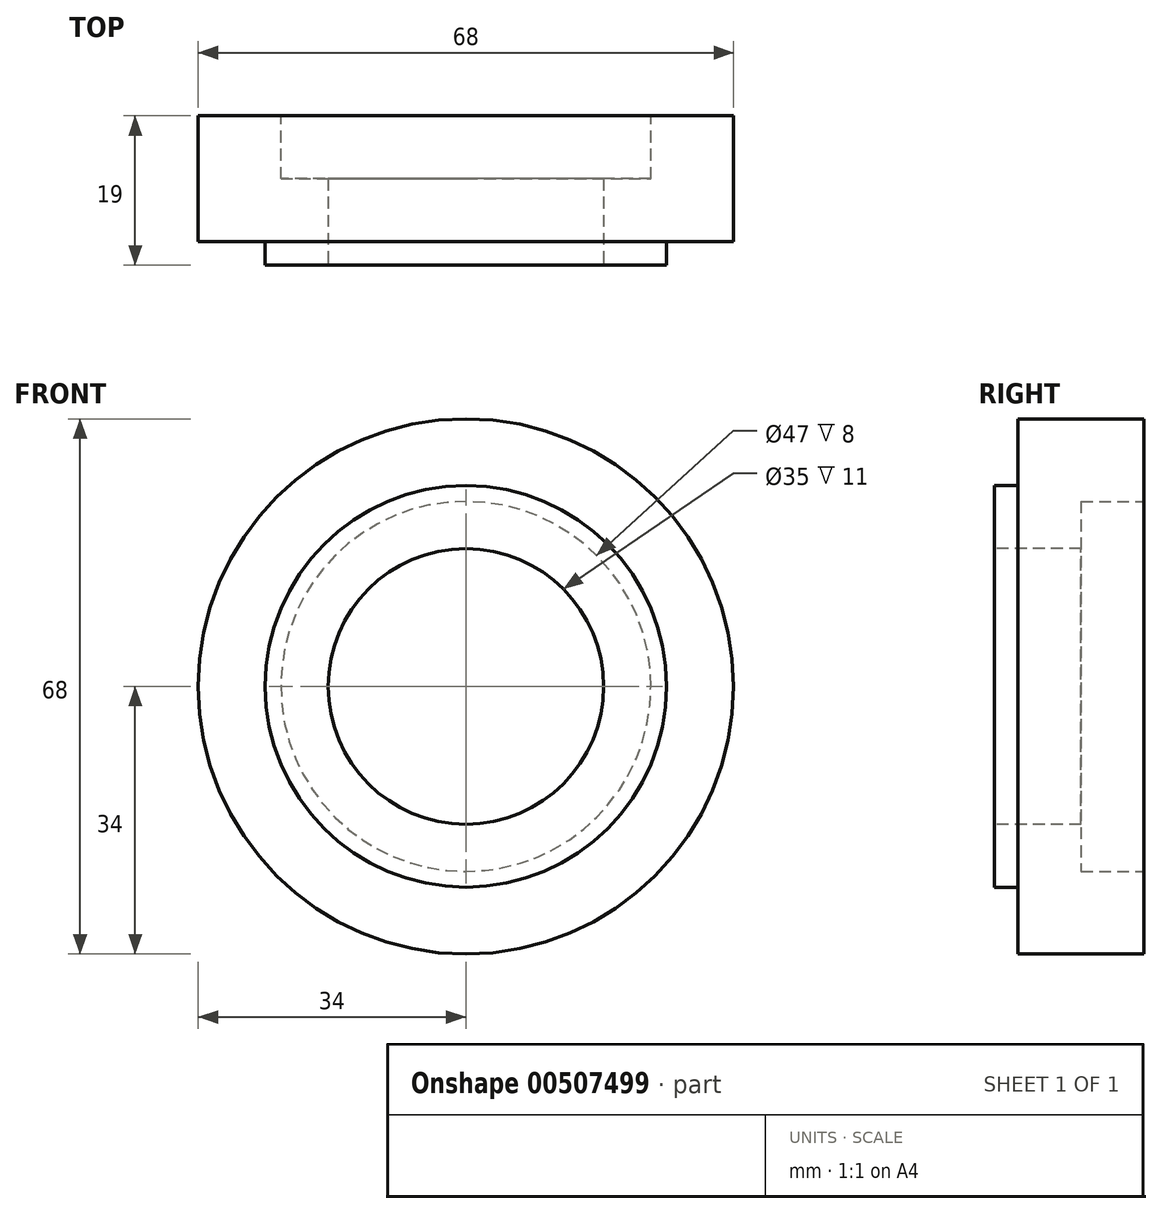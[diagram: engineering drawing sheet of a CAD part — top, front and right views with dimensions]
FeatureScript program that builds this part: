
annotation { "Feature Type Name" : "Feature", "Feature Type Description" : "" }
export const myFeature = defineFeature(function(context is Context, id is Id, definition is map)
    precondition{}
    {
        {
            var Q0;
            Q0=qCreatedBy(makeId("Front.planeOp"),FACE);
            var sketch = newSketch(context, id + "F0", { "sketchPlane" : qUnion([Q0])});
            skCircle(sketch, "E0", {"center": v(0, 0) * mm, "radius": 34 * mm});
            skSolve(sketch);
        }
        {
            var Q0;
            Q0 = qSketchRegion(id + "F0", true);
            extrude(context, id + "F1", {"entities" : qUnion([Q0]), "depth" : 16 * mm});
        }
        {
            var Q0;
            Q0=makeQuery(id+"F1.opExtrude","CAP_FACE",FACE,{"disambiguationData":[OSD([sQuery(id+"F0.wireOp",EDGE,"E0")])],"isStart":false});
            var sketch = newSketch(context, id + "F2", { "sketchPlane" : qUnion([Q0])});
            skCircle(sketch, "E1", {"center": v(0, 0) * mm, "radius": 25.5 * mm});
            skSolve(sketch);
        }
        {
            var Q0;
            Q0 = qSketchRegion(id + "F2", true);
            extrude(context, id + "F3", {"entities" : qUnion([Q0]), "operationType" : NewBodyOperationType.ADD, "depth" : 3 * mm});
        }
        {
            var Q0;
            Q0=makeQuery(id+"F1.opExtrude","CAP_FACE",FACE,{"disambiguationData":[OSD([sQuery(id+"F0.wireOp",EDGE,"E0")])],"isStart":true});
            var sketch = newSketch(context, id + "F4", { "sketchPlane" : qUnion([Q0])});
            skCircle(sketch, "E2", {"center": v(0, 0) * mm, "radius": 23.5 * mm});
            skSolve(sketch);
        }
        {
            var Q0;
            Q0 = qSketchRegion(id + "F4", true);
            extrude(context, id + "F5", {"entities" : qUnion([Q0]), "operationType" : NewBodyOperationType.REMOVE, "oppositeDirection" : true, "depth" : 8 * mm});
        }
        {
            var Q0;
            Q0=makeQuery(id+"F3.opExtrude","CAP_FACE",FACE,{"disambiguationData":[OSD([sQuery(id+"F2.wireOp",EDGE,"E1")])],"isStart":false});
            var sketch = newSketch(context, id + "F6", { "sketchPlane" : qUnion([Q0])});
            skCircle(sketch, "E3", {"center": v(0, 0) * mm, "radius": 17.5 * mm});
            skSolve(sketch);
        }
        {
            var Q0;
            Q0 = qSketchRegion(id + "F6", true);
            extrude(context, id + "F7", {"entities" : qUnion([Q0]), "operationType" : NewBodyOperationType.REMOVE, "oppositeDirection" : true, "depth" : 11 * mm});
        }
    });
